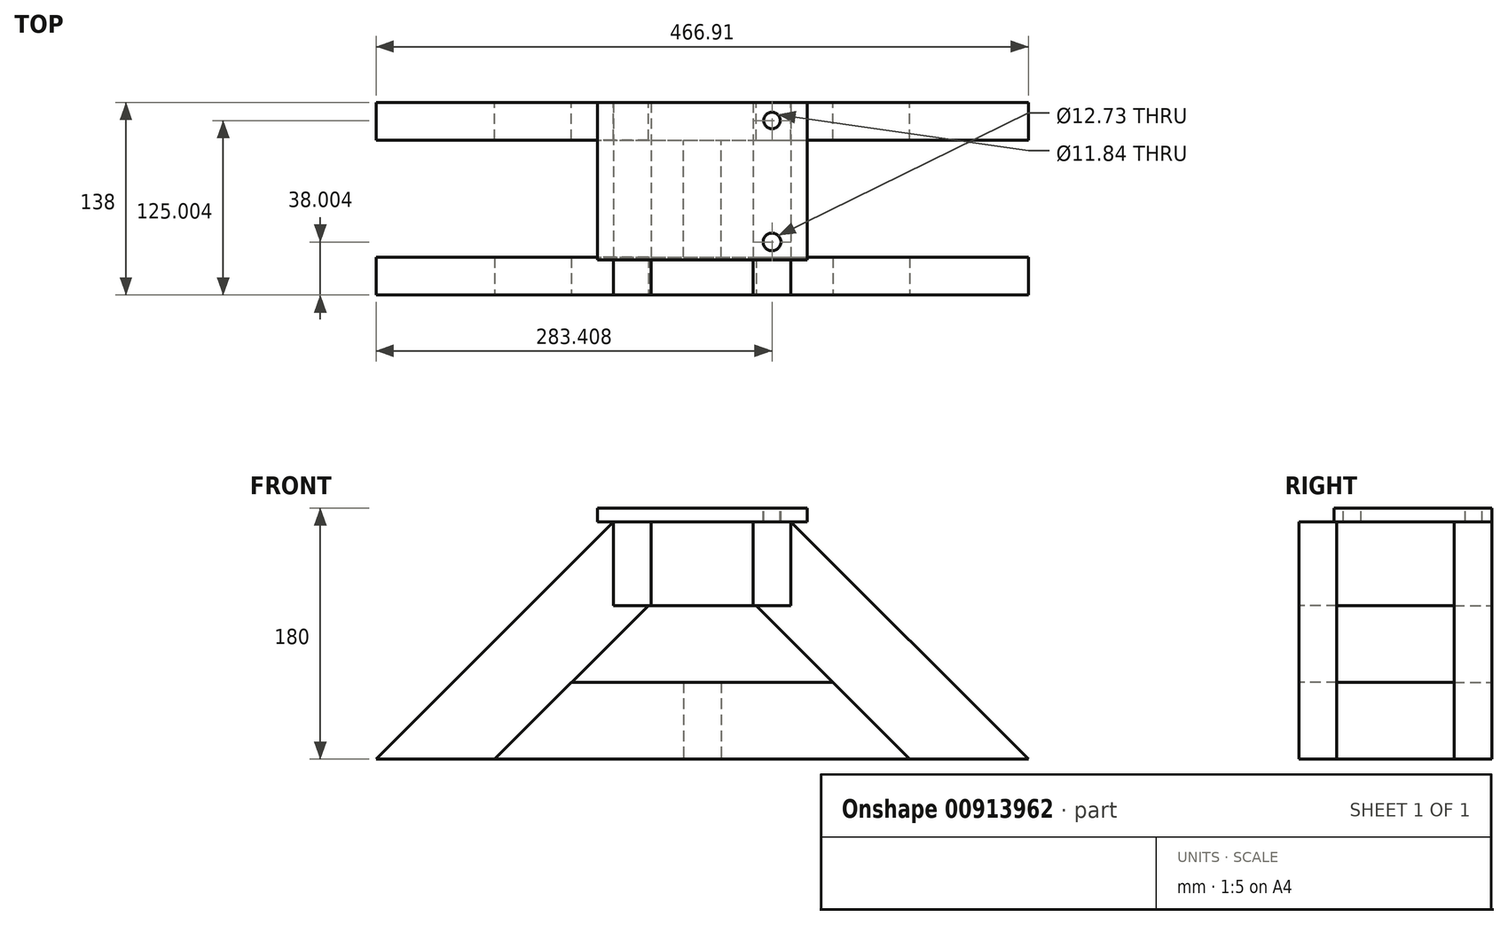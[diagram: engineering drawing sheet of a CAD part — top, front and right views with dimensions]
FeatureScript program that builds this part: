
annotation { "Feature Type Name" : "Feature", "Feature Type Description" : "" }
export const myFeature = defineFeature(function(context is Context, id is Id, definition is map)
    precondition{}
    {
        {
            assignVariable(context, id + "F0", {"name" : "breite", "anyValue" : 27});
        }
        {
            assignVariable(context, id + "F1", {"name" : "hoehe", "anyValue" : 60});
        }
        {
            var Q0;
            Q0=qCreatedBy(makeId("Top.planeOp"),FACE);
            var sketch = newSketch(context, id + "F2", { "sketchPlane" : qUnion([Q0])});
            skLineSegment(sketch, "E0.bottom", {"start": v(-125.44, 63.16) * mm, "end": v(24.56, 63.16) * mm});
            skLineSegment(sketch, "E0.top", {"start": v(-125.44, 36.16) * mm, "end": v(24.56, 36.16) * mm});
            skLineSegment(sketch, "E0.left", {"start": v(-125.44, 63.16) * mm, "end": v(-125.44, 36.16) * mm});
            skLineSegment(sketch, "E0.right", {"start": v(24.56, 63.16) * mm, "end": v(24.56, 36.16) * mm});
            skLineSegment(sketch, "E1.bottom", {"start": v(-125.44, -22.84) * mm, "end": v(24.56, -22.84) * mm});
            skLineSegment(sketch, "E1.top", {"start": v(-125.44, -49.84) * mm, "end": v(24.56, -49.84) * mm});
            skLineSegment(sketch, "E1.left", {"start": v(-125.44, -22.84) * mm, "end": v(-125.44, -49.84) * mm});
            skLineSegment(sketch, "E1.right", {"start": v(24.56, -22.84) * mm, "end": v(24.56, -49.84) * mm});
            skCircle(sketch, "E2", {"center": v(-0.44, 50.16) * mm, "radius": 5.92 * mm});
            skCircle(sketch, "E3", {"center": v(-0.44, -36.84) * mm, "radius": 6.37 * mm});
            skSolve(sketch);
        }
        {
            var Q0;
            Q0 = qSketchRegion(id + "F2", true);
            extrude(context, id + "F3", {"entities" : qUnion([Q0]), "depth" : (getVariable(context, 'hoehe')) * mm, "offsetDistance" : 25 * mm});
        }
        {
            var Q0;
            Q0=makeQuery(id+"F3.opExtrude","CAP_FACE",FACE,{"disambiguationData":[OSD([sQuery(id+"F2.wireOp",EDGE,"E1.bottom"),sQuery(id+"F2.wireOp",EDGE,"E1.top"),sQuery(id+"F2.wireOp",EDGE,"E1.left"),sQuery(id+"F2.wireOp",EDGE,"E1.right"),sQuery(id+"F2.wireOp",EDGE,"E3")])],"isStart":true});
            var sketch = newSketch(context, id + "F4", { "sketchPlane" : qUnion([Q0])});
            skLineSegment(sketch, "E4.bottom", {"start": v(-125.44, 49.84) * mm, "end": v(24.65, 49.84) * mm});
            skLineSegment(sketch, "E4.top", {"start": v(-125.44, -63.16) * mm, "end": v(24.65, -63.16) * mm});
            skLineSegment(sketch, "E4.left", {"start": v(-125.44, 49.84) * mm, "end": v(-125.44, -63.16) * mm});
            skLineSegment(sketch, "E4.right", {"start": v(24.65, 49.84) * mm, "end": v(24.65, -63.16) * mm});
            skCircle(sketch, "E5.0", {"center": v(-0.44, 36.84) * mm, "radius": 6.37 * mm});
            skCircle(sketch, "E5.1", {"center": v(-0.44, -50.16) * mm, "radius": 5.92 * mm});
            skSolve(sketch);
        }
        {
            var Q0;
            Q0 = qSketchRegion(id + "F4", true);
            extrude(context, id + "F5", {"entities" : qUnion([Q0]), "depth" : 10 * mm, "offsetDistance" : 25 * mm});
        }
        {
            var Q0;
            Q0=makeQuery(id+"F3.opExtrude","SWEPT_BODY",BODY,{"disambiguationData":[OSD([sQuery(id+"F2.wireOp",EDGE,"E1.bottom"),sQuery(id+"F2.wireOp",EDGE,"E1.top"),sQuery(id+"F2.wireOp",EDGE,"E1.left"),sQuery(id+"F2.wireOp",EDGE,"E1.right"),sQuery(id+"F2.wireOp",EDGE,"E3")])]});
            var Q1;
            Q1=makeQuery(id+"F3.opExtrude","SWEPT_BODY",BODY,{"disambiguationData":[OSD([sQuery(id+"F2.wireOp",EDGE,"E0.bottom"),sQuery(id+"F2.wireOp",EDGE,"E0.top"),sQuery(id+"F2.wireOp",EDGE,"E0.left"),sQuery(id+"F2.wireOp",EDGE,"E0.right"),sQuery(id+"F2.wireOp",EDGE,"E2")])]});
            deleteBodies(context, id + "F6", {"entities" : qUnion([Q0, Q1])});
        }
        {
            var Q0;
            Q0=makeQuery(id+"F5.opExtrude","CAP_FACE",FACE,{"disambiguationData":[OSD([sQuery(id+"F4.wireOp",EDGE,"E4.bottom"),sQuery(id+"F4.wireOp",EDGE,"E4.top"),sQuery(id+"F4.wireOp",EDGE,"E4.left"),sQuery(id+"F4.wireOp",EDGE,"E4.right"),sQuery(id+"F4.wireOp",EDGE,"E5.0"),sQuery(id+"F4.wireOp",EDGE,"E5.1")])],"isStart":false});
            var sketch = newSketch(context, id + "F7", { "sketchPlane" : qUnion([Q0])});
            skLineSegment(sketch, "E6.bottom", {"start": v(-13.94, -63.16) * mm, "end": v(13.06, -63.16) * mm});
            skLineSegment(sketch, "E6.top", {"start": v(-13.94, 74.84) * mm, "end": v(13.06, 74.84) * mm});
            skLineSegment(sketch, "E6.left", {"start": v(-13.94, -63.16) * mm, "end": v(-13.94, 74.84) * mm});
            skLineSegment(sketch, "E6.right", {"start": v(13.06, -63.16) * mm, "end": v(13.06, 74.84) * mm});
            skPoint(sketch, "E7", {"position": v(-0.44, 36.84) * mm});
            skPoint(sketch, "E8", {"position": v(-0.44, -50.16) * mm});
            skLineSegment(sketch, "E9", {"start": v(-50.4, 49.84) * mm, "end": v(-50.4, -63.16) * mm, "construction": true});
            skLineSegment(sketch, "E10.MirrorCS", {"start": v(-86.85, 74.84) * mm, "end": v(-113.85, 74.84) * mm});
            skLineSegment(sketch, "E11.MirrorCS", {"start": v(-86.85, -63.16) * mm, "end": v(-86.85, 74.84) * mm});
            skPoint(sketch, "E12.MirrorP", {"position": v(-100.35, -50.16) * mm});
            skLineSegment(sketch, "E13.MirrorCS", {"start": v(-86.85, -63.16) * mm, "end": v(-113.85, -63.16) * mm});
            skPoint(sketch, "E14.MirrorP", {"position": v(-100.35, 36.84) * mm});
            skLineSegment(sketch, "E15.MirrorCS", {"start": v(-113.85, -63.16) * mm, "end": v(-113.85, 74.84) * mm});
            skSolve(sketch);
        }
        {
            var Q0;
            Q0 = qSketchRegion(id + "F7", true);
            extrude(context, id + "F8", {"entities" : qUnion([Q0]), "depth" : (getVariable(context, 'hoehe')) * mm, "offsetDistance" : 25 * mm});
        }
        {
            var Q0;
            Q0=makeQuery(id+"F8.opExtrude","SWEPT_FACE",FACE,{"disambiguationData":[OSD([sQuery(id+"F7.wireOp",EDGE,"E6.top")])]});
            var sketch = newSketch(context, id + "F9", { "sketchPlane" : qUnion([Q0])});
            skLineSegment(sketch, "E16", {"start": v(-13.94, -180) * mm, "end": v(132.24, -180) * mm, "construction": true});
            skLineSegment(sketch, "E17", {"start": v(13.06, -10) * mm, "end": v(183.06, -180) * mm});
            skLineSegment(sketch, "E18.0", {"start": v(-11.8, -70) * mm, "end": v(98.2, -180) * mm});
            skLineSegment(sketch, "E19", {"start": v(-11.8, -70) * mm, "end": v(13.06, -70) * mm});
            skLineSegment(sketch, "E20", {"start": v(13.06, -70) * mm, "end": v(13.06, -10) * mm});
            skLineSegment(sketch, "E21", {"start": v(98.2, -180) * mm, "end": v(183.06, -180) * mm});
            skSolve(sketch);
        }
        {
            var Q0;
            Q0 = qSketchRegion(id + "F9", true);
            extrude(context, id + "F10", {"entities" : qUnion([Q0]), "oppositeDirection" : true, "depth" : (getVariable(context, 'breite')) * mm, "offsetDistance" : 25 * mm});
        }
        {
            var Q0;
            Q0=makeQuery(id+"F8.opExtrude","SWEPT_FACE",FACE,{"disambiguationData":[OSD([sQuery(id+"F7.wireOp",EDGE,"E10.MirrorCS")])]});
            var sketch = newSketch(context, id + "F11", { "sketchPlane" : qUnion([Q0])});
            skLineSegment(sketch, "E22", {"start": v(-113.85, -180) * mm, "end": v(-1139.55, -180) * mm, "construction": true});
            skLineSegment(sketch, "E23", {"start": v(-113.85, -10) * mm, "end": v(-283.85, -180) * mm});
            skLineSegment(sketch, "E24", {"start": v(-199, -180) * mm, "end": v(-89, -70) * mm});
            skLineSegment(sketch, "E25", {"start": v(-283.85, -180) * mm, "end": v(-199, -180) * mm});
            skLineSegment(sketch, "E26", {"start": v(-89, -70) * mm, "end": v(-113.85, -70) * mm});
            skLineSegment(sketch, "E27", {"start": v(-113.85, -70) * mm, "end": v(-113.85, -10) * mm});
            skSolve(sketch);
        }
        {
            var Q0;
            Q0 = qSketchRegion(id + "F11", true);
            extrude(context, id + "F12", {"entities" : qUnion([Q0]), "oppositeDirection" : true, "depth" : (getVariable(context, 'breite')) * mm, "offsetDistance" : 25 * mm});
        }
        {
            var Q0;
            Q0=makeQuery(id+"F12.opExtrude","CAP_FACE",FACE,{"disambiguationData":[OSD([sQuery(id+"F11.wireOp",EDGE,"E23"),sQuery(id+"F11.wireOp",EDGE,"E24"),sQuery(id+"F11.wireOp",EDGE,"E25"),sQuery(id+"F11.wireOp",EDGE,"E26"),sQuery(id+"F11.wireOp",EDGE,"E27")])],"isStart":true});
            var sketch = newSketch(context, id + "F13", { "sketchPlane" : qUnion([Q0])});
            skLineSegment(sketch, "E28", {"start": v(-199, -180) * mm, "end": v(98.2, -180) * mm});
            skLineSegment(sketch, "E29", {"start": v(-144, -125) * mm, "end": v(43.2, -125) * mm});
            skLineSegment(sketch, "E30", {"start": v(43.2, -125) * mm, "end": v(98.2, -180) * mm});
            skSolve(sketch);
        }
        {
            var Q0;
            {var subQ0=sQuery(id+"F13.wireOp",EDGE,"E28");Q0=makeQuery(id+"F13.imprint","IMPRINT",FACE,{"disambiguationData":[TD([[makeQuery(id+"F13.imprint","IMPRINT",EDGE,{"derivedFrom":subQ0}),1.0]])]});}
            extrude(context, id + "F14", {"entities" : qUnion([Q0]), "oppositeDirection" : true, "depth" : (getVariable(context, 'breite')) * mm, "offsetDistance" : 25 * mm});
        }
        {
            var Q0;
            Q0=makeQuery(id+"F14.opExtrude","CAP_FACE",FACE,{"disambiguationData":[OSD([sQuery(id+"F11.wireOp",EDGE,"E24"),sQuery(id+"F13.wireOp",EDGE,"E28"),sQuery(id+"F13.wireOp",EDGE,"E29"),sQuery(id+"F13.wireOp",EDGE,"E30")])],"isStart":true});
            cPlane(context, id + "F15", {"entities" : qUnion([Q0]), "cplaneType" : CPlaneType.OFFSET, "offset" : (138 / 2) * mm, "oppositeDirection" : true, "width" : 150 * mm, "height" : 150 * mm});
        }
        {
            var Q0;
            Q0=makeQuery(id+"F12.opExtrude","SWEPT_BODY",BODY,{"disambiguationData":[OSD([sQuery(id+"F11.wireOp",EDGE,"E23"),sQuery(id+"F11.wireOp",EDGE,"E24"),sQuery(id+"F11.wireOp",EDGE,"E25"),sQuery(id+"F11.wireOp",EDGE,"E26"),sQuery(id+"F11.wireOp",EDGE,"E27")])]});
            var Q1;
            Q1=makeQuery(id+"F14.opExtrude","SWEPT_BODY",BODY,{"disambiguationData":[OSD([sQuery(id+"F11.wireOp",EDGE,"E24"),sQuery(id+"F13.wireOp",EDGE,"E28"),sQuery(id+"F13.wireOp",EDGE,"E29"),sQuery(id+"F13.wireOp",EDGE,"E30")])]});
            var Q2;
            Q2=makeQuery(id+"F10.opExtrude","SWEPT_BODY",BODY,{"disambiguationData":[OSD([sQuery(id+"F9.wireOp",EDGE,"E17"),sQuery(id+"F9.wireOp",EDGE,"E18.0"),sQuery(id+"F9.wireOp",EDGE,"E19"),sQuery(id+"F9.wireOp",EDGE,"E20"),sQuery(id+"F9.wireOp",EDGE,"E21")])]});
            var Q3;
            Q3=qCreatedBy(id+"F15.planeOp",FACE);
            mirror(context, id + "F16", {"entities" : qUnion([Q0, Q1, Q2]), "mirrorPlane" : qUnion([Q3])});
        }
        {
            var Q0;
            Q0=makeQuery(id+"F16.opPattern","COPY",FACE,{"derivedFrom":makeQuery(id+"F14.opExtrude","CAP_FACE",FACE,{"disambiguationData":[OSD([sQuery(id+"F11.wireOp",EDGE,"E24"),sQuery(id+"F13.wireOp",EDGE,"E28"),sQuery(id+"F13.wireOp",EDGE,"E29"),sQuery(id+"F13.wireOp",EDGE,"E30")])],"isStart":false}),"instanceName":"1"});
            var sketch = newSketch(context, id + "F17", { "sketchPlane" : qUnion([Q0])});
            skLineSegment(sketch, "E31.bottom", {"start": v(-63.9, -125) * mm, "end": v(-36.9, -125) * mm});
            skLineSegment(sketch, "E31.top", {"start": v(-63.9, -180) * mm, "end": v(-36.9, -180) * mm});
            skLineSegment(sketch, "E31.left", {"start": v(-63.9, -125) * mm, "end": v(-63.9, -180) * mm});
            skLineSegment(sketch, "E31.right", {"start": v(-36.9, -125) * mm, "end": v(-36.9, -180) * mm});
            skPoint(sketch, "E32", {"position": v(-50.4, -180) * mm});
            skSolve(sketch);
        }
        {
            var Q0;
            Q0=makeQuery(id+"F17.imprint","IMPRINT",FACE,{"disambiguationData":[TD([[makeQuery(id+"F17.imprint","IMPRINT",EDGE,{"derivedFrom":sQuery(id+"F17.wireOp",EDGE,"E31.bottom")}),-1.0]])]});
            extrude(context, id + "F18", {"entities" : qUnion([Q0]), "endBound" : BoundingType.UP_TO_NEXT, "depth" : 25 * mm, "offsetDistance" : 25 * mm});
        }
        {
            var Q0;
            Q0=makeQuery(id+"F8.opExtrude","SWEPT_FACE",FACE,{"disambiguationData":[OSD([sQuery(id+"F7.wireOp",EDGE,"E6.left")])]});
            var sketch = newSketch(context, id + "F19", { "sketchPlane" : qUnion([Q0])});
            skLineSegment(sketch, "E33.bottom", {"start": v(74.84, -10) * mm, "end": v(47.84, -10) * mm});
            skLineSegment(sketch, "E33.top", {"start": v(74.84, -70) * mm, "end": v(47.84, -70) * mm});
            skLineSegment(sketch, "E33.left", {"start": v(74.84, -10) * mm, "end": v(74.84, -70) * mm});
            skLineSegment(sketch, "E33.right", {"start": v(47.84, -10) * mm, "end": v(47.84, -70) * mm});
            skLineSegment(sketch, "E34.bottom", {"start": v(-63.16, -10) * mm, "end": v(-36.16, -10) * mm});
            skLineSegment(sketch, "E34.top", {"start": v(-63.16, -70) * mm, "end": v(-36.16, -70) * mm});
            skLineSegment(sketch, "E34.left", {"start": v(-63.16, -10) * mm, "end": v(-63.16, -70) * mm});
            skLineSegment(sketch, "E34.right", {"start": v(-36.16, -10) * mm, "end": v(-36.16, -70) * mm});
            skSolve(sketch);
        }
        {
            var Q0;
            Q0 = qSketchRegion(id + "F19", true);
            extrude(context, id + "F20", {"entities" : qUnion([Q0]), "endBound" : BoundingType.UP_TO_NEXT, "depth" : 25 * mm, "offsetDistance" : 25 * mm});
        }
    });
